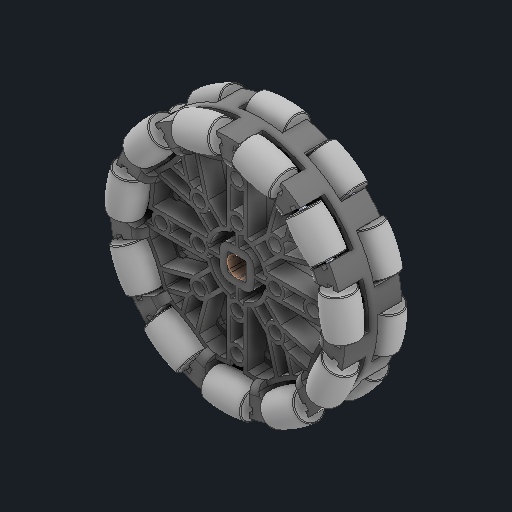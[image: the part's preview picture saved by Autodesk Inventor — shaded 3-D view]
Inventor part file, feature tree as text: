
AUTODESK INVENTOR PART (.ipt)
format: ipt  version: 2024 (Build 280153000, 153)  size: 3,346,944 bytes
history: native  units: in
note: dims shown in document units (in); Inventor stores cm internally (conversion verified against a paired STEP export)
features: other x49, sketch x1
ambient origin geometry x8: Origin, YZ Plane, XZ Plane, XY Plane, X Axis, Y Axis, Z Axis, Center Point
bodies: Solid1 (feature_tree), Solid2 (feature_tree), Solid3 (feature_tree), Solid4 (feature_tree), Solid5 (feature_tree), Solid6 (feature_tree), Solid7 (feature_tree), Solid8 (feature_tree), Solid9 (feature_tree), Solid10 (feature_tree), Solid11 (feature_tree), Solid12 (feature_tree), Solid13 (feature_tree), Solid14 (feature_tree), Solid15 (feature_tree), Solid16 (feature_tree), Solid17 (feature_tree), Solid18 (feature_tree), Solid19 (feature_tree), Solid20 (feature_tree), Solid21 (feature_tree), Solid22 (feature_tree), Solid23 (feature_tree), Solid24 (feature_tree), Solid25 (feature_tree), Solid26 (feature_tree), Solid27 (feature_tree), Solid28 (feature_tree), Solid29 (feature_tree), Solid30 (feature_tree), Solid31 (feature_tree), Solid32 (feature_tree), Solid33 (feature_tree), Solid34 (feature_tree), Solid35 (feature_tree), Solid36 (feature_tree), Solid37 (feature_tree), Solid38 (feature_tree), Solid39 (feature_tree), Solid40 (feature_tree), Solid41 (feature_tree), Solid42 (feature_tree), Solid43 (feature_tree), Solid44 (feature_tree), Solid45 (feature_tree)
feature tree (50):
  other  "3.25 Omni Antistatic.ipt"
  other  "Solid1::3.25 Omni Antistatic.ipt"
  other  "Solid2::3.25 Omni Antistatic.ipt"
  other  "Solid3::3.25 Omni Antistatic.ipt"
  other  "Solid4::3.25 Omni Antistatic.ipt"
  other  "Solid5::3.25 Omni Antistatic.ipt"
  other  "Solid6::3.25 Omni Antistatic.ipt"
  other  "Solid7::3.25 Omni Antistatic.ipt"
  other  "Solid8::3.25 Omni Antistatic.ipt"
  other  "Solid9::3.25 Omni Antistatic.ipt"
  other  "Solid10::3.25 Omni Antistatic.ipt"
  other  "Solid11::3.25 Omni Antistatic.ipt"
  other  "Solid12::3.25 Omni Antistatic.ipt"
  other  "Solid13::3.25 Omni Antistatic.ipt"
  other  "Solid14::3.25 Omni Antistatic.ipt"
  other  "Solid15::3.25 Omni Antistatic.ipt"
  other  "Solid16::3.25 Omni Antistatic.ipt"
  other  "Solid17::3.25 Omni Antistatic.ipt"
  other  "Solid18::3.25 Omni Antistatic.ipt"
  other  "Solid19::3.25 Omni Antistatic.ipt"
  other  "Solid20::3.25 Omni Antistatic.ipt"
  other  "Solid21::3.25 Omni Antistatic.ipt"
  other  "Solid22::3.25 Omni Antistatic.ipt"
  other  "Solid23::3.25 Omni Antistatic.ipt"
  other  "Solid24::3.25 Omni Antistatic.ipt"
  other  "Solid25::3.25 Omni Antistatic.ipt"
  other  "Solid26::3.25 Omni Antistatic.ipt"
  other  "Solid27::3.25 Omni Antistatic.ipt"
  other  "Solid28::3.25 Omni Antistatic.ipt"
  other  "Solid29::3.25 Omni Antistatic.ipt"
  other  "Solid30::3.25 Omni Antistatic.ipt"
  other  "Solid31::3.25 Omni Antistatic.ipt"
  other  "Solid32::3.25 Omni Antistatic.ipt"
  other  "Solid33::3.25 Omni Antistatic.ipt"
  other  "Solid34::3.25 Omni Antistatic.ipt"
  other  "Solid35::3.25 Omni Antistatic.ipt"
  other  "Solid36::3.25 Omni Antistatic.ipt"
  other  "Solid37::3.25 Omni Antistatic.ipt"
  other  "Solid38::3.25 Omni Antistatic.ipt"
  other  "Solid39::3.25 Omni Antistatic.ipt"
  other  "Solid40::3.25 Omni Antistatic.ipt"
  other  "Solid41::3.25 Omni Antistatic.ipt"
  other  "Solid42::3.25 Omni Antistatic.ipt"
  other  "Solid43::3.25 Omni Antistatic.ipt"
  other  "Solid44::3.25 Omni Antistatic.ipt"
  other  "Solid45::3.25 Omni Antistatic.ipt"
  other  "TaggingFeature1"
  sketch  "Sketch1"  dims[d0=0.3937in]
  other  "Srf1"
  other  "Srf1::Derived"
